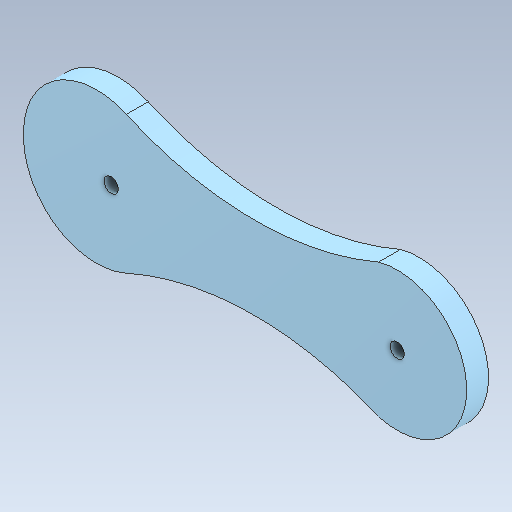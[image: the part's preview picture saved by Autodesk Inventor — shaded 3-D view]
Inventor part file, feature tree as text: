
AUTODESK INVENTOR PART (.ipt)
format: ipt  version: 2020.3 (Build 243373000, 373)  size: 179,712 bytes
history: native  units: in
note: dims shown in document units (in); Inventor stores cm internally (conversion verified against a paired STEP export)
features: other x4, sketch x1, direct_edit x1, fillet x1
ambient origin geometry x8: Origin, YZ Plane, XZ Plane, XY Plane, X Axis, Y Axis, Z Axis, Center Point
bodies: Solid1 (feature_tree)
feature tree (7):
  other  "Part 18.ipt"
  sketch  "Sketch1"  dims[d1=0.1969in d2=0.7874in]
  direct_edit  "Direct Edit1"
  fillet  "Fillet1"  Radius=0.7874in
  other  "Solid1::Part 18.ipt"
  other  "TaggingFeature1"
  other  "Size1"
